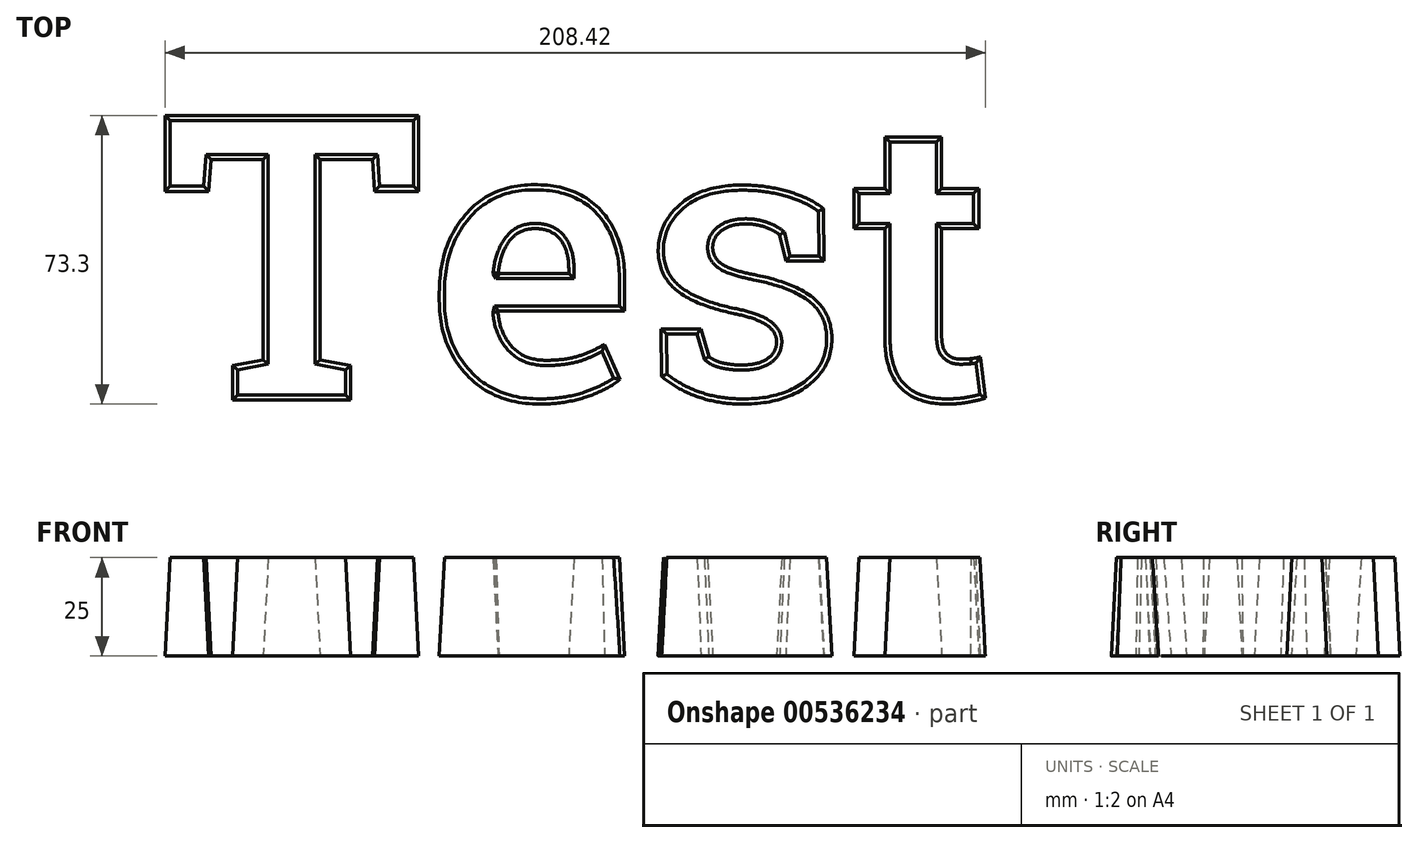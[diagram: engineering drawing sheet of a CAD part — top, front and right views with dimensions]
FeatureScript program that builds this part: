
annotation { "Feature Type Name" : "Feature", "Feature Type Description" : "" }
export const myFeature = defineFeature(function(context is Context, id is Id, definition is map)
    precondition{}
    {
        {
            var Q0;
            Q0=qCreatedBy(makeId("Top.planeOp"),FACE);
            var sketch = newSketch(context, id + "F0", { "sketchPlane" : qUnion([Q0])});
            skText(sketch, "E0", { "text": "Test", "fontName": "RobotoSlab-Bold.ttf"});
            const initialGuessF0  = {"E0": [-0.09707, -0.04466, 1, 0, 0.07317]};
            skSetInitialGuess(sketch, initialGuessF0);
            skSolve(sketch);
        }
        {
            var Q0;
            Q0 = qSketchRegion(id + "F0", true);
            extrude(context, id + "F1", {"entities" : qUnion([Q0]), "depth" : 25 * mm, "offsetDistance" : 25 * mm, "hasDraft" : true, "draftAngle" : 3 * degree, "draftPullDirection" : true});
        }
    });
